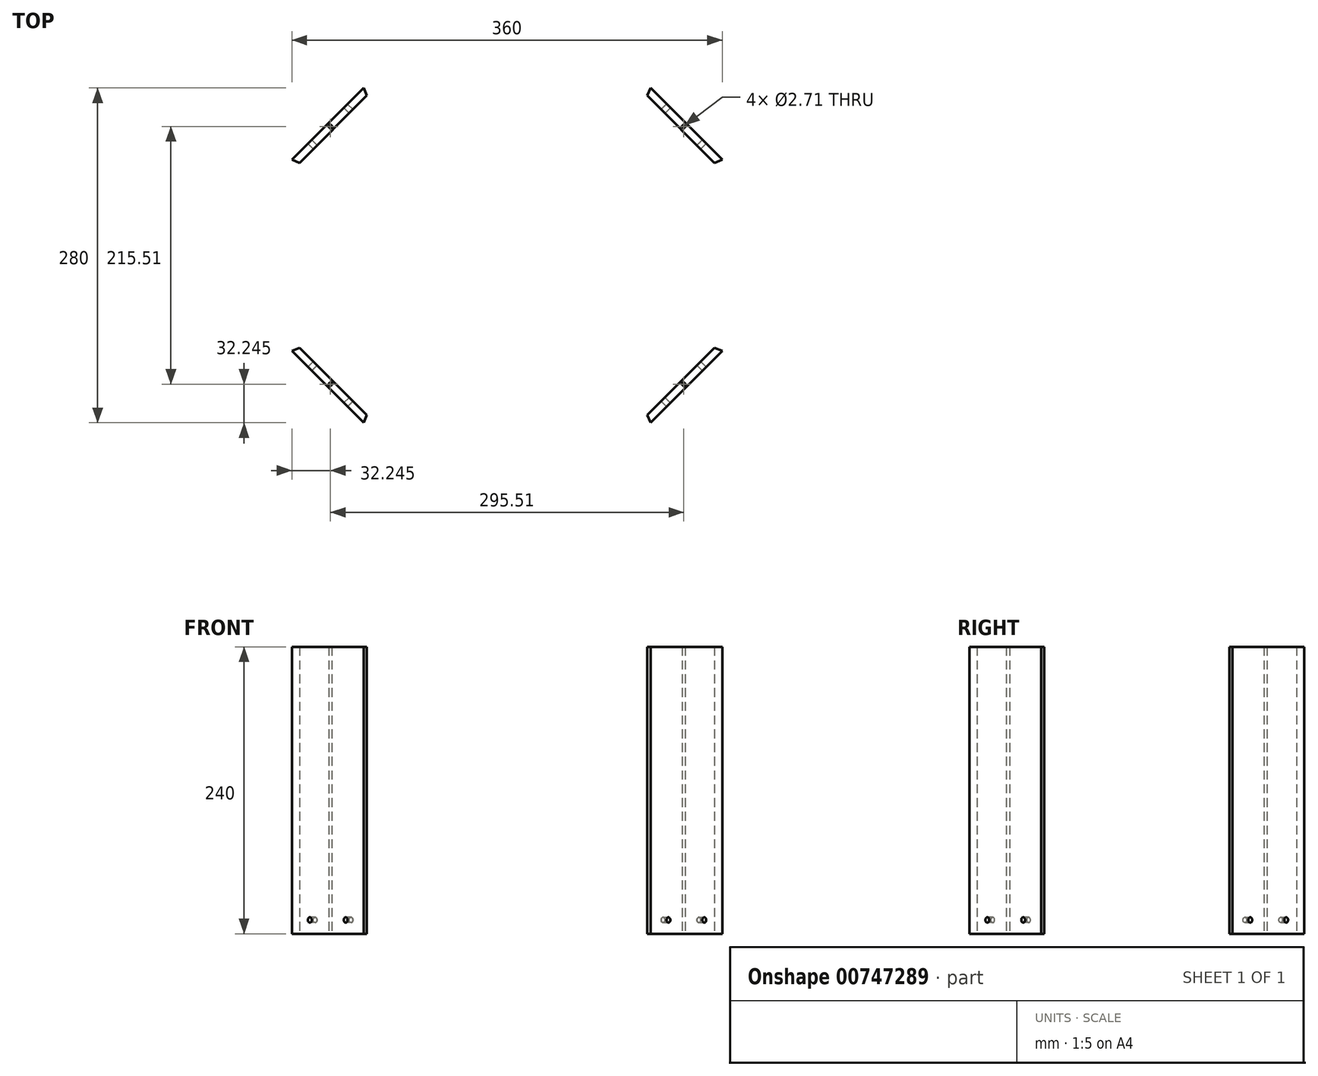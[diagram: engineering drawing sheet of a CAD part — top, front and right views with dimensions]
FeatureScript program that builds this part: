
annotation { "Feature Type Name" : "Feature", "Feature Type Description" : "" }
export const myFeature = defineFeature(function(context is Context, id is Id, definition is map)
    precondition{}
    {
        {
            var Q0;
            Q0=qCreatedBy(makeId("Top.planeOp"),FACE);
            var sketch = newSketch(context, id + "F0", { "sketchPlane" : qUnion([Q0])});
            skLineSegment(sketch, "E0", {"start": v(-120, 0) * mm, "end": v(-180, 60) * mm});
            skLineSegment(sketch, "E1", {"start": v(-180, 60) * mm, "end": v(-180, 220) * mm});
            skLineSegment(sketch, "E2", {"start": v(-180, 220) * mm, "end": v(-120, 280) * mm});
            skLineSegment(sketch, "E3", {"start": v(-120, 280) * mm, "end": v(120, 280) * mm});
            skLineSegment(sketch, "E4", {"start": v(120, 280) * mm, "end": v(180, 220) * mm});
            skLineSegment(sketch, "E5", {"start": v(180, 220) * mm, "end": v(180, 60) * mm});
            skLineSegment(sketch, "E6", {"start": v(180, 60) * mm, "end": v(120, 0) * mm});
            skLineSegment(sketch, "E7", {"start": v(120, 0) * mm, "end": v(-120, 0) * mm});
            skLineSegment(sketch, "E8.0", {"start": v(-173.65, 62.63) * mm, "end": v(-173.65, 217.37) * mm});
            skLineSegment(sketch, "E8.1", {"start": v(-117.37, 6.35) * mm, "end": v(-173.65, 62.63) * mm});
            skLineSegment(sketch, "E8.2", {"start": v(-173.65, 217.37) * mm, "end": v(-117.37, 273.65) * mm});
            skLineSegment(sketch, "E8.3", {"start": v(117.37, 6.35) * mm, "end": v(-117.37, 6.35) * mm});
            skLineSegment(sketch, "E8.4", {"start": v(-117.37, 273.65) * mm, "end": v(117.37, 273.65) * mm});
            skLineSegment(sketch, "E8.5", {"start": v(117.37, 273.65) * mm, "end": v(173.65, 217.37) * mm});
            skLineSegment(sketch, "E8.6", {"start": v(173.65, 217.37) * mm, "end": v(173.65, 62.63) * mm});
            skLineSegment(sketch, "E8.7", {"start": v(173.65, 62.63) * mm, "end": v(117.37, 6.35) * mm});
            skLineSegment(sketch, "E9", {"start": v(-120, 0) * mm, "end": v(-117.37, 6.35) * mm});
            skLineSegment(sketch, "E10", {"start": v(-120, 280) * mm, "end": v(-117.37, 273.65) * mm});
            skLineSegment(sketch, "E11", {"start": v(120, 280) * mm, "end": v(117.37, 273.65) * mm});
            skLineSegment(sketch, "E12", {"start": v(120, 0) * mm, "end": v(117.37, 6.35) * mm});
            skLineSegment(sketch, "E13", {"start": v(-173.65, 217.37) * mm, "end": v(-180, 220) * mm});
            skLineSegment(sketch, "E14", {"start": v(-173.65, 62.63) * mm, "end": v(-180, 60) * mm});
            skLineSegment(sketch, "E15", {"start": v(173.65, 62.63) * mm, "end": v(180, 60) * mm});
            skLineSegment(sketch, "E16", {"start": v(173.65, 217.37) * mm, "end": v(180, 220) * mm});
            skSolve(sketch);
        }
        {
            var Q0;
            Q0=makeQuery(id+"F0.imprint","IMPRINT",FACE,{"disambiguationData":[TD([[makeQuery(id+"F0.imprint","IMPRINT",EDGE,{"derivedFrom":sQuery(id+"F0.wireOp",EDGE,"E0")}),-1.0]])]});
            extrude(context, id + "F1", {"entities" : qUnion([Q0]), "depth" : 240 * mm, "offsetDistance" : 25 * mm});
        }
        {
            var Q0;
            Q0=makeQuery(id+"F0.imprint","IMPRINT",FACE,{"disambiguationData":[TD([[makeQuery(id+"F0.imprint","IMPRINT",EDGE,{"derivedFrom":sQuery(id+"F0.wireOp",EDGE,"E2")}),-1.0]])]});
            extrude(context, id + "F2", {"entities" : qUnion([Q0]), "depth" : 240 * mm, "offsetDistance" : 25 * mm});
        }
        {
            var Q0;
            Q0=makeQuery(id+"F0.imprint","IMPRINT",FACE,{"disambiguationData":[TD([[makeQuery(id+"F0.imprint","IMPRINT",EDGE,{"derivedFrom":sQuery(id+"F0.wireOp",EDGE,"E4")}),-1.0]])]});
            extrude(context, id + "F3", {"entities" : qUnion([Q0]), "depth" : 240 * mm, "offsetDistance" : 25 * mm});
        }
        {
            var Q0;
            Q0=makeQuery(id+"F0.imprint","IMPRINT",FACE,{"disambiguationData":[TD([[makeQuery(id+"F0.imprint","IMPRINT",EDGE,{"derivedFrom":sQuery(id+"F0.wireOp",EDGE,"E6")}),-1.0]])]});
            extrude(context, id + "F4", {"entities" : qUnion([Q0]), "depth" : 240 * mm, "offsetDistance" : 25 * mm});
        }
        {
            var Q0;
            Q0=makeQuery(id+"F1.opExtrude","SWEPT_FACE",FACE,{"disambiguationData":[OSD([sQuery(id+"F0.wireOp",EDGE,"E0")])]});
            var sketch = newSketch(context, id + "F5", { "sketchPlane" : qUnion([Q0])});
            skLineSegment(sketch, "E17", {"start": v(-169.7, 0) * mm, "end": v(-84.85, 0) * mm, "construction": true});
            skLineSegment(sketch, "E18", {"start": v(-84.85, 0) * mm, "end": v(-127.28, 0) * mm, "construction": true});
            skLineSegment(sketch, "E19", {"start": v(-127.28, 0) * mm, "end": v(-106.07, 0) * mm, "construction": true});
            skLineSegment(sketch, "E20", {"start": v(-106.07, 0) * mm, "end": v(-106.07, 11.51) * mm, "construction": true});
            skLineSegment(sketch, "E21", {"start": v(-127.28, 0) * mm, "end": v(-169.7, 0) * mm, "construction": true});
            skLineSegment(sketch, "E22", {"start": v(-148.5, 0) * mm, "end": v(-148.5, 11.51) * mm, "construction": true});
            skSolve(sketch);
        }
        {
            var Q0;
            Q0=makeQuery(id+"F4.opExtrude","SWEPT_FACE",FACE,{"disambiguationData":[OSD([sQuery(id+"F0.wireOp",EDGE,"E6")])]});
            var sketch = newSketch(context, id + "F6", { "sketchPlane" : qUnion([Q0])});
            skLineSegment(sketch, "E23", {"start": v(84.85, 0) * mm, "end": v(169.7, 0) * mm, "construction": true});
            skLineSegment(sketch, "E24", {"start": v(169.7, 0) * mm, "end": v(127.28, 0) * mm, "construction": true});
            skLineSegment(sketch, "E25", {"start": v(127.28, 0) * mm, "end": v(148.5, 0) * mm, "construction": true});
            skLineSegment(sketch, "E26", {"start": v(148.5, 0) * mm, "end": v(148.5, 11.51) * mm, "construction": true});
            skLineSegment(sketch, "E27", {"start": v(84.85, 0) * mm, "end": v(127.28, 0) * mm, "construction": true});
            skLineSegment(sketch, "E28", {"start": v(106.07, 0) * mm, "end": v(106.07, 11.51) * mm, "construction": true});
            skSolve(sketch);
        }
        {
            var Q0;
            Q0=makeQuery(id+"F3.opExtrude","SWEPT_FACE",FACE,{"disambiguationData":[OSD([sQuery(id+"F0.wireOp",EDGE,"E4")])]});
            var sketch = newSketch(context, id + "F7", { "sketchPlane" : qUnion([Q0])});
            skLineSegment(sketch, "E29", {"start": v(28.28, 0) * mm, "end": v(113.14, 0) * mm, "construction": true});
            skLineSegment(sketch, "E30", {"start": v(113.14, 0) * mm, "end": v(70.71, 0) * mm, "construction": true});
            skLineSegment(sketch, "E31", {"start": v(70.71, 0) * mm, "end": v(91.92, 0) * mm, "construction": true});
            skLineSegment(sketch, "E32", {"start": v(91.92, 0) * mm, "end": v(91.92, 11.51) * mm, "construction": true});
            skLineSegment(sketch, "E33", {"start": v(28.28, 0) * mm, "end": v(70.71, 0) * mm, "construction": true});
            skLineSegment(sketch, "E34", {"start": v(49.5, 0) * mm, "end": v(49.5, 11.51) * mm, "construction": true});
            skSolve(sketch);
        }
        {
            var Q0;
            Q0=makeQuery(id+"F2.opExtrude","SWEPT_FACE",FACE,{"disambiguationData":[OSD([sQuery(id+"F0.wireOp",EDGE,"E2")])]});
            var sketch = newSketch(context, id + "F8", { "sketchPlane" : qUnion([Q0])});
            skLineSegment(sketch, "E35", {"start": v(-113.14, 0) * mm, "end": v(-28.28, 0) * mm, "construction": true});
            skLineSegment(sketch, "E36", {"start": v(-28.28, 0) * mm, "end": v(-70.71, 0) * mm, "construction": true});
            skLineSegment(sketch, "E37", {"start": v(-70.71, 0) * mm, "end": v(-49.5, 0) * mm, "construction": true});
            skLineSegment(sketch, "E38", {"start": v(-49.5, 0) * mm, "end": v(-49.5, 11.51) * mm, "construction": true});
            skLineSegment(sketch, "E39", {"start": v(-113.14, 0) * mm, "end": v(-70.71, 0) * mm, "construction": true});
            skLineSegment(sketch, "E40", {"start": v(-91.92, 0) * mm, "end": v(-91.92, 11.51) * mm, "construction": true});
            skSolve(sketch);
        }
        {
            var Q0;
            Q0=sQuery(id+"F8.wireOp",VERTEX,"E40.end");
            var Q1;
            Q1=sQuery(id+"F8.wireOp",VERTEX,"E38.end");
            var Q2;
            Q2=sQuery(id+"F5.wireOp",VERTEX,"E20.end");
            var Q3;
            Q3=sQuery(id+"F5.wireOp",VERTEX,"E22.end");
            var Q4;
            Q4=sQuery(id+"F6.wireOp",VERTEX,"E26.end");
            var Q5;
            Q5=sQuery(id+"F6.wireOp",VERTEX,"E28.end");
            var Q6;
            Q6=sQuery(id+"F7.wireOp",VERTEX,"E34.end");
            var Q7;
            Q7=sQuery(id+"F7.wireOp",VERTEX,"E32.end");
            var Q8;
            Q8=makeQuery(id+"F2.opExtrude","SWEPT_BODY",BODY,{"disambiguationData":[OSD([sQuery(id+"F0.wireOp",EDGE,"E2"),sQuery(id+"F0.wireOp",EDGE,"E8.2"),sQuery(id+"F0.wireOp",EDGE,"E10"),sQuery(id+"F0.wireOp",EDGE,"E13")])]});
            var Q9;
            Q9=makeQuery(id+"F1.opExtrude","SWEPT_BODY",BODY,{"disambiguationData":[OSD([sQuery(id+"F0.wireOp",EDGE,"E0"),sQuery(id+"F0.wireOp",EDGE,"E8.1"),sQuery(id+"F0.wireOp",EDGE,"E9"),sQuery(id+"F0.wireOp",EDGE,"E14")])]});
            var Q10;
            Q10=makeQuery(id+"F4.opExtrude","SWEPT_BODY",BODY,{"disambiguationData":[OSD([sQuery(id+"F0.wireOp",EDGE,"E6"),sQuery(id+"F0.wireOp",EDGE,"E8.7"),sQuery(id+"F0.wireOp",EDGE,"E12"),sQuery(id+"F0.wireOp",EDGE,"E15")])]});
            var Q11;
            Q11=makeQuery(id+"F3.opExtrude","SWEPT_BODY",BODY,{"disambiguationData":[OSD([sQuery(id+"F0.wireOp",EDGE,"E4"),sQuery(id+"F0.wireOp",EDGE,"E8.5"),sQuery(id+"F0.wireOp",EDGE,"E11"),sQuery(id+"F0.wireOp",EDGE,"E16")])]});
            hole(context, id + "F9", {"style" : HoleStyle.SIMPLE, "endStyle" : HoleEndStyle.BLIND, "holeDiameter" : 4.5 * mm, "majorDiameter" : 5 * mm, "holeDepth" : 12 * mm, "isTappedThrough" : true, "tappedDepth" : 12 * mm, "tapClearance" : 3, "locations" : qUnion([Q0, Q1, Q2, Q3, Q4, Q5, Q6, Q7]), "scope" : qUnion([Q8, Q9, Q10, Q11])});
        }
        {
            var Q0;
            Q0=makeQuery(id+"F1.opExtrude","CAP_FACE",FACE,{"disambiguationData":[OSD([sQuery(id+"F0.wireOp",EDGE,"E0"),sQuery(id+"F0.wireOp",EDGE,"E8.1"),sQuery(id+"F0.wireOp",EDGE,"E9"),sQuery(id+"F0.wireOp",EDGE,"E14")])],"isStart":true});
            var sketch = newSketch(context, id + "F10", { "sketchPlane" : qUnion([Q0])});
            skLineSegment(sketch, "E41", {"start": v(-150, -30) * mm, "end": v(-147.75, -32.25) * mm, "construction": true});
            skSolve(sketch);
        }
        {
            var Q0;
            Q0=makeQuery(id+"F4.opExtrude","CAP_FACE",FACE,{"disambiguationData":[OSD([sQuery(id+"F0.wireOp",EDGE,"E6"),sQuery(id+"F0.wireOp",EDGE,"E8.7"),sQuery(id+"F0.wireOp",EDGE,"E12"),sQuery(id+"F0.wireOp",EDGE,"E15")])],"isStart":true});
            var sketch = newSketch(context, id + "F11", { "sketchPlane" : qUnion([Q0])});
            skLineSegment(sketch, "E42", {"start": v(150, -30) * mm, "end": v(147.75, -32.25) * mm, "construction": true});
            skSolve(sketch);
        }
        {
            var Q0;
            Q0=makeQuery(id+"F2.opExtrude","CAP_FACE",FACE,{"disambiguationData":[OSD([sQuery(id+"F0.wireOp",EDGE,"E2"),sQuery(id+"F0.wireOp",EDGE,"E8.2"),sQuery(id+"F0.wireOp",EDGE,"E10"),sQuery(id+"F0.wireOp",EDGE,"E13")])],"isStart":true});
            var sketch = newSketch(context, id + "F12", { "sketchPlane" : qUnion([Q0])});
            skLineSegment(sketch, "E43", {"start": v(-150, -250) * mm, "end": v(-147.75, -247.75) * mm, "construction": true});
            skSolve(sketch);
        }
        {
            var Q0;
            Q0=makeQuery(id+"F3.opExtrude","CAP_FACE",FACE,{"disambiguationData":[OSD([sQuery(id+"F0.wireOp",EDGE,"E4"),sQuery(id+"F0.wireOp",EDGE,"E8.5"),sQuery(id+"F0.wireOp",EDGE,"E11"),sQuery(id+"F0.wireOp",EDGE,"E16")])],"isStart":true});
            var sketch = newSketch(context, id + "F13", { "sketchPlane" : qUnion([Q0])});
            skLineSegment(sketch, "E44", {"start": v(150, -250) * mm, "end": v(147.75, -247.75) * mm, "construction": true});
            skSolve(sketch);
        }
        {
            var Q0;
            Q0=sQuery(id+"F13.wireOp",VERTEX,"E44.end");
            var Q1;
            Q1=sQuery(id+"F11.wireOp",VERTEX,"E42.end");
            var Q2;
            Q2=sQuery(id+"F10.wireOp",VERTEX,"E41.end");
            var Q3;
            Q3=sQuery(id+"F12.wireOp",VERTEX,"E43.end");
            var Q4;
            Q4=makeQuery(id+"F1.opExtrude","SWEPT_BODY",BODY,{"disambiguationData":[OSD([sQuery(id+"F0.wireOp",EDGE,"E0"),sQuery(id+"F0.wireOp",EDGE,"E8.1"),sQuery(id+"F0.wireOp",EDGE,"E9"),sQuery(id+"F0.wireOp",EDGE,"E14")])]});
            var Q5;
            Q5=makeQuery(id+"F2.opExtrude","SWEPT_BODY",BODY,{"disambiguationData":[OSD([sQuery(id+"F0.wireOp",EDGE,"E2"),sQuery(id+"F0.wireOp",EDGE,"E8.2"),sQuery(id+"F0.wireOp",EDGE,"E10"),sQuery(id+"F0.wireOp",EDGE,"E13")])]});
            var Q6;
            Q6=makeQuery(id+"F3.opExtrude","SWEPT_BODY",BODY,{"disambiguationData":[OSD([sQuery(id+"F0.wireOp",EDGE,"E4"),sQuery(id+"F0.wireOp",EDGE,"E8.5"),sQuery(id+"F0.wireOp",EDGE,"E11"),sQuery(id+"F0.wireOp",EDGE,"E16")])]});
            var Q7;
            Q7=makeQuery(id+"F4.opExtrude","SWEPT_BODY",BODY,{"disambiguationData":[OSD([sQuery(id+"F0.wireOp",EDGE,"E6"),sQuery(id+"F0.wireOp",EDGE,"E8.7"),sQuery(id+"F0.wireOp",EDGE,"E12"),sQuery(id+"F0.wireOp",EDGE,"E15")])]});
            hole(context, id + "F14", {"style" : HoleStyle.SIMPLE, "endStyle" : HoleEndStyle.THROUGH, "standardTappedOrClearance" : lookupTablePath({ "standard" : "ANSI", "engagement" : "75%", "pitch" : "32 tpi", "size" : "#6", "type" : "Tapped" }), "standardBlindInLast" : lookupTablePath({ "standard" : "ANSI", "engagement" : "75%", "pitch" : "32 tpi", "size" : "#6", "type" : "Tapped" }), "holeDiameter" : 2.7 * mm, "majorDiameter" : 3.5 * mm, "showTappedDepth" : true, "isTappedThrough" : true, "tappedDepth" : 12 * mm, "tapClearance" : 3, "locations" : qUnion([Q0, Q1, Q2, Q3]), "scope" : qUnion([Q4, Q5, Q6, Q7])});
        }
    });
